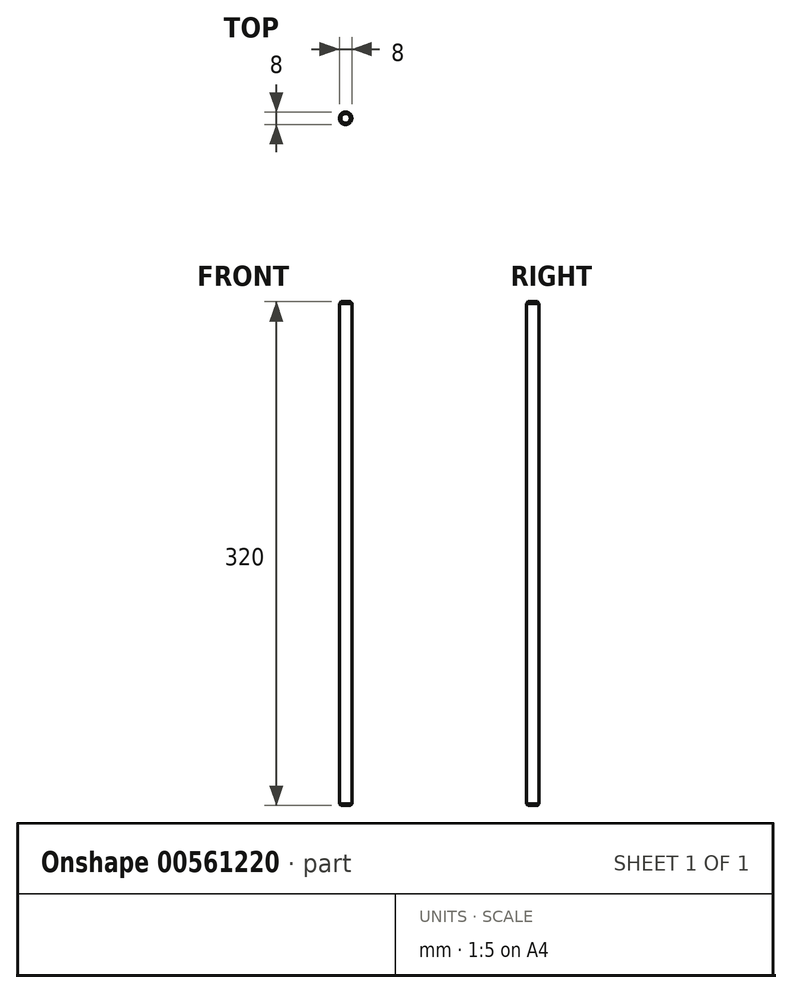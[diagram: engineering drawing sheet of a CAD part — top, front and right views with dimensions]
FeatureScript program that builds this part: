
annotation { "Feature Type Name" : "Feature", "Feature Type Description" : "" }
export const myFeature = defineFeature(function(context is Context, id is Id, definition is map)
    precondition{}
    {
        {
            var Q0;
            Q0=qCreatedBy(makeId("Top.planeOp"),FACE);
            var sketch = newSketch(context, id + "F0", { "sketchPlane" : qUnion([Q0])});
            skCircle(sketch, "E0", {"center": v(0, 0) * mm, "radius": 4 * mm});
            skSolve(sketch);
        }
        {
            var Q0;
            Q0=qSketchRegion(id+"F0",true);
            extrude(context, id + "F1", {"entities" : qUnion([Q0]), "endBound" : BoundingType.SYMMETRIC, "depth" : 320 * mm, "offsetDistance" : 25 * mm});
        }
        {
            var Q0;
            Q0=makeQuery(id+"F1.opExtrude","CAP_EDGE",EDGE,{"disambiguationData":[OSD([sQuery(id+"F0.wireOp",EDGE,"E0")])],"isStart":false});
            var Q1;
            Q1=makeQuery(id+"F1.opExtrude","CAP_EDGE",EDGE,{"disambiguationData":[OSD([sQuery(id+"F0.wireOp",EDGE,"E0")])],"isStart":true});
            chamfer(context, id + "F2", {"entities" : qUnion([Q0, Q1]), "width" : 1 * mm, "tangentPropagation" : true});
        }
    });
